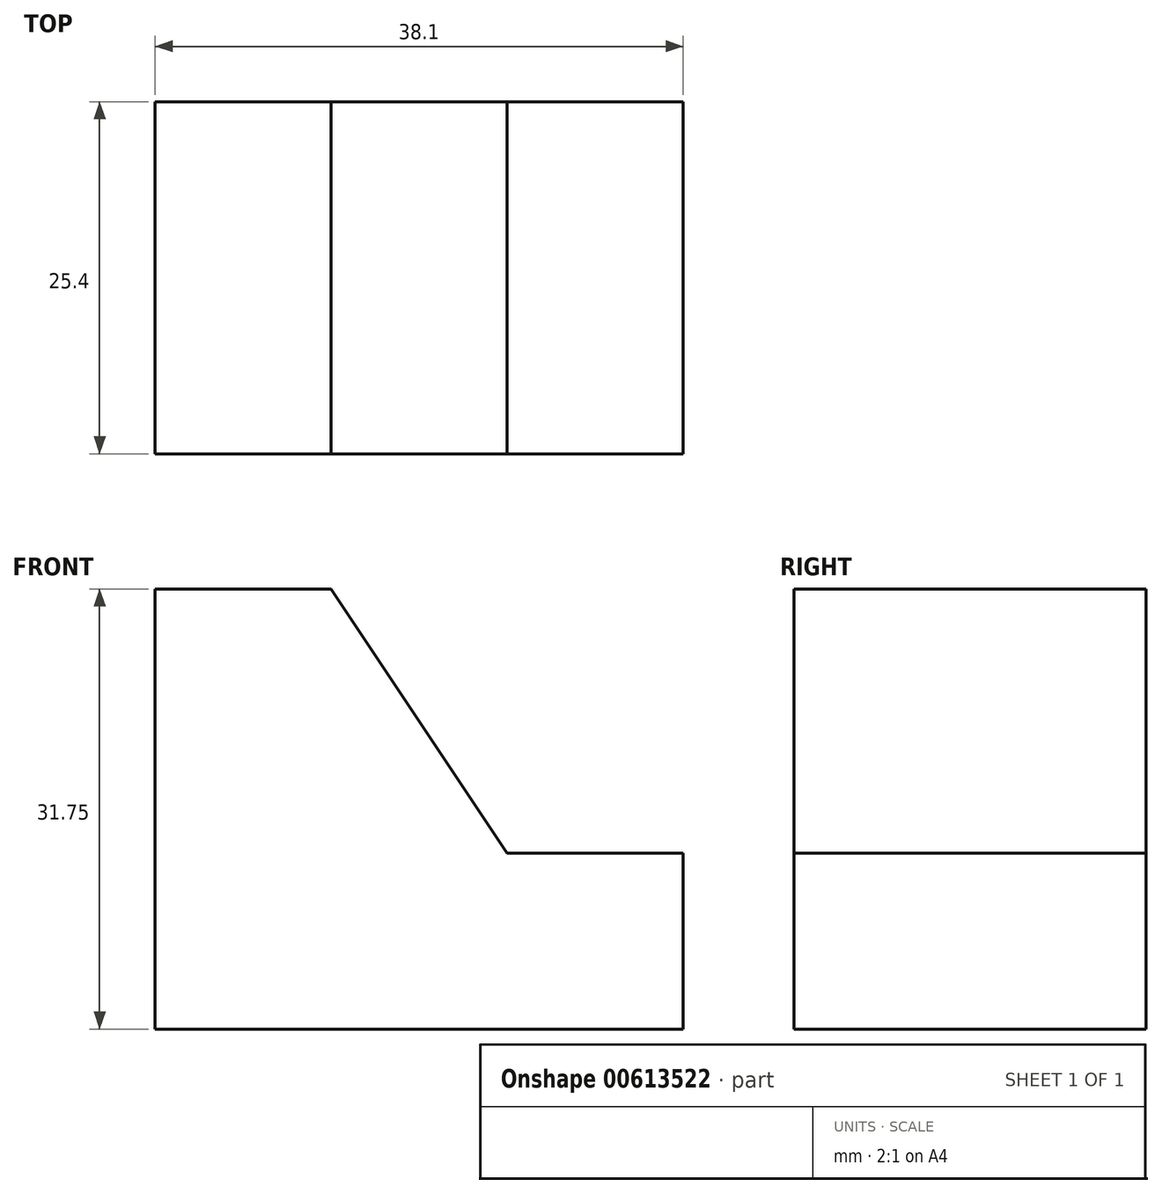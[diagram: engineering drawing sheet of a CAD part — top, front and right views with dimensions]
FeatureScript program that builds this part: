
annotation { "Feature Type Name" : "Feature", "Feature Type Description" : "" }
export const myFeature = defineFeature(function(context is Context, id is Id, definition is map)
    precondition{}
    {
        {
            var Q0;
            Q0=qCreatedBy(makeId("Front.planeOp"),FACE);
            var sketch = newSketch(context, id + "F0", { "sketchPlane" : qUnion([Q0])});
            skLineSegment(sketch, "E0", {"start": v(0, 0) * mm, "end": v(12.7, 0) * mm});
            skLineSegment(sketch, "E1", {"start": v(12.7, 0) * mm, "end": v(12.7, -12.7) * mm});
            skLineSegment(sketch, "E2", {"start": v(12.7, -12.7) * mm, "end": v(-25.4, -12.7) * mm});
            skLineSegment(sketch, "E3", {"start": v(-25.4, -12.7) * mm, "end": v(-25.4, 19.05) * mm});
            skLineSegment(sketch, "E4", {"start": v(-25.4, 19.05) * mm, "end": v(-12.7, 19.05) * mm});
            skLineSegment(sketch, "E5", {"start": v(-12.7, 19.05) * mm, "end": v(0, 0) * mm});
            skSolve(sketch);
        }
        {
            var Q0;
            Q0=makeQuery(id+"F0.imprint","IMPRINT",FACE,{"disambiguationData":[TD([[makeQuery(id+"F0.imprint","IMPRINT",EDGE,{"derivedFrom":sQuery(id+"F0.wireOp",EDGE,"E0")}),-1.0]])]});
            extrude(context, id + "F1", {"entities" : qUnion([Q0]), "depth" : 25.4 * mm, "offsetDistance" : 25.4 * mm});
        }
    });
